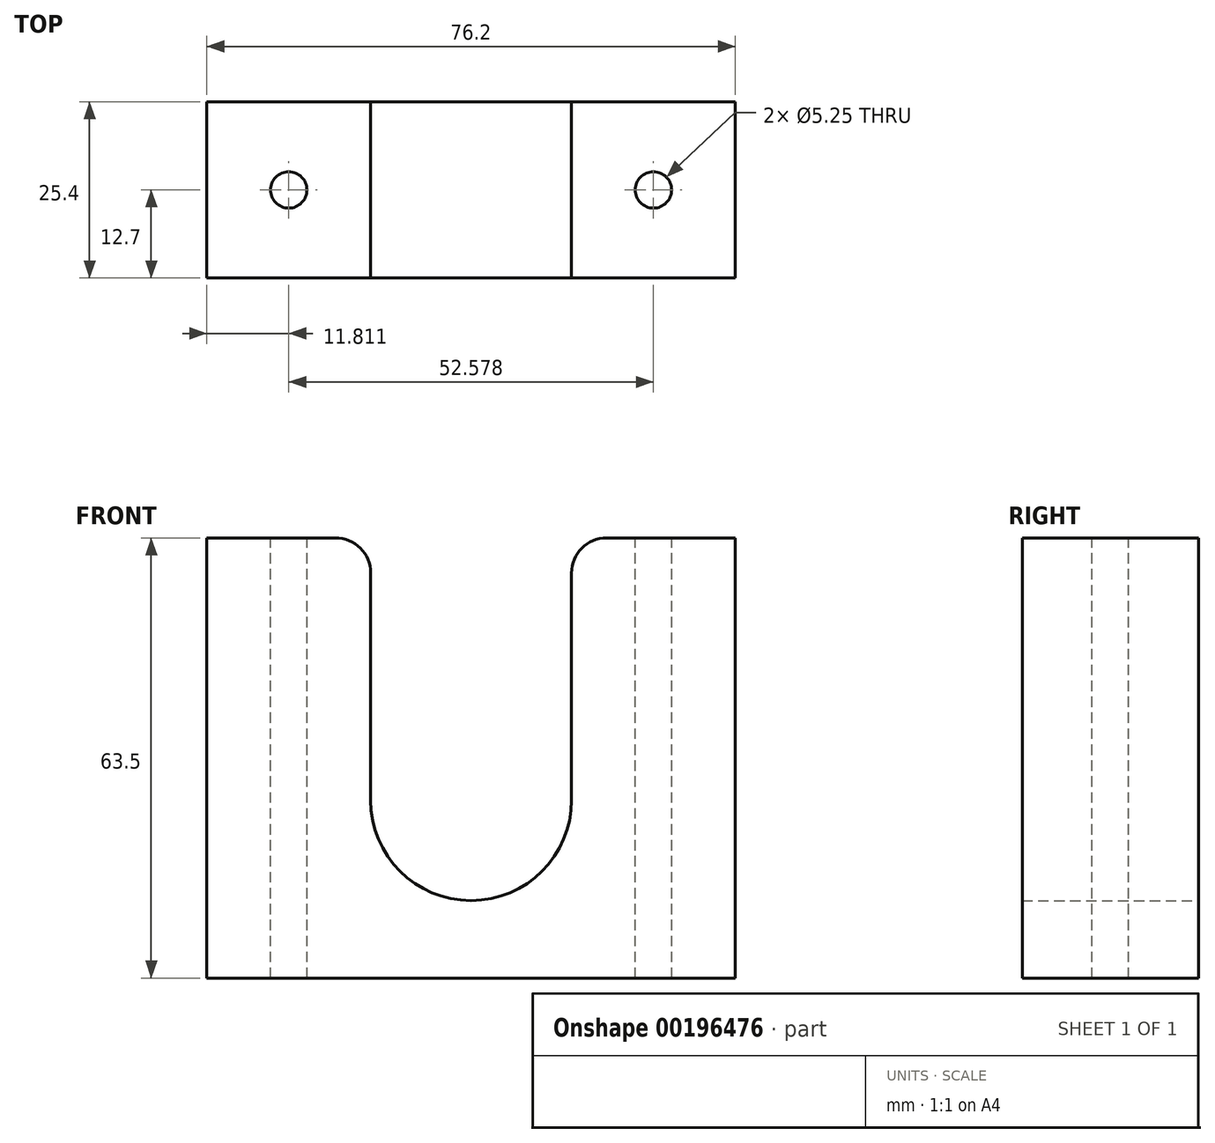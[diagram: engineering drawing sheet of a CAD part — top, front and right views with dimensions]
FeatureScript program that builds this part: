
annotation { "Feature Type Name" : "Feature", "Feature Type Description" : "" }
export const myFeature = defineFeature(function(context is Context, id is Id, definition is map)
    precondition{}
    {
        {
            var Q0;
            Q0=qCreatedBy(makeId("Front.planeOp"),FACE);
            var sketch = newSketch(context, id + "F0", { "sketchPlane" : qUnion([Q0])});
            skLineSegment(sketch, "E0.bottom", {"start": v(0, 0) * mm, "end": v(76.2, 0) * mm});
            skLineSegment(sketch, "E0.left", {"start": v(0, 0) * mm, "end": v(0, 63.5) * mm});
            skLineSegment(sketch, "E0.right", {"start": v(76.2, 0) * mm, "end": v(76.2, 63.5) * mm});
            skLineSegment(sketch, "E1", {"start": v(0, 63.5) * mm, "end": v(23.62, 63.5) * mm});
            skLineSegment(sketch, "E2", {"start": v(76.2, 63.5) * mm, "end": v(52.58, 63.5) * mm});
            skLineSegment(sketch, "E3", {"start": v(23.62, 63.5) * mm, "end": v(23.62, 25.65) * mm});
            skLineSegment(sketch, "E4", {"start": v(52.58, 63.5) * mm, "end": v(52.58, 25.65) * mm});
            skArc(sketch, "E5", {"start": v(23.62, 25.65) * mm, "mid": v(38.1, 11.18) * mm, "end": v(52.58, 25.65) * mm});
            skSolve(sketch);
        }
        {
            var Q0;
            Q0 = qSketchRegion(id + "F0", true);
            extrude(context, id + "F1", {"entities" : qUnion([Q0]), "depth" : 25.4 * mm});
        }
        {
            var Q0;
            Q0=makeQuery(id+"F1.opExtrude","SWEPT_FACE",FACE,{"disambiguationData":[OSD([sQuery(id+"F0.wireOp",EDGE,"E1")])]});
            var sketch = newSketch(context, id + "F2", { "sketchPlane" : qUnion([Q0])});
            skLineSegment(sketch, "E6", {"start": v(0, 0) * mm, "end": v(23.62, -25.4) * mm, "construction": true});
            skLineSegment(sketch, "E7", {"start": v(23.62, 0) * mm, "end": v(0, -25.4) * mm, "construction": true});
            skPoint(sketch, "E8", {"position": v(11.81, -12.7) * mm});
            skSolve(sketch);
        }
        {
            var Q0;
            Q0=makeQuery(id+"F1.opExtrude","SWEPT_FACE",FACE,{"disambiguationData":[OSD([sQuery(id+"F0.wireOp",EDGE,"E2")])]});
            var sketch = newSketch(context, id + "F3", { "sketchPlane" : qUnion([Q0])});
            skLineSegment(sketch, "E9", {"start": v(52.58, 0) * mm, "end": v(76.2, -25.4) * mm, "construction": true});
            skLineSegment(sketch, "E10", {"start": v(76.2, 0) * mm, "end": v(52.58, -25.4) * mm, "construction": true});
            skPoint(sketch, "E11", {"position": v(64.39, -12.7) * mm});
            skSolve(sketch);
        }
        {
            var Q0;
            Q0=sQuery(id+"F2.wireOp",VERTEX,"E8");
            var Q1;
            Q1=sQuery(id+"F3.wireOp",VERTEX,"E11");
            var Q2;
            Q2=makeQuery(id+"F1.opExtrude","SWEPT_BODY",BODY,{"disambiguationData":[OSD([sQuery(id+"F0.wireOp",EDGE,"E0.bottom"),sQuery(id+"F0.wireOp",EDGE,"E0.left"),sQuery(id+"F0.wireOp",EDGE,"E0.right"),sQuery(id+"F0.wireOp",EDGE,"E1"),sQuery(id+"F0.wireOp",EDGE,"E2"),sQuery(id+"F0.wireOp",EDGE,"E3"),sQuery(id+"F0.wireOp",EDGE,"E4"),sQuery(id+"F0.wireOp",EDGE,"E5")])]});
            hole(context, id + "F4", {"style" : HoleStyle.SIMPLE, "endStyle" : HoleEndStyle.THROUGH, "standardTappedOrClearance" : lookupTablePath({ "standard" : "ISO", "engagement" : "75%", "pitch" : "0.75 mm", "size" : "M6", "type" : "Tapped" }), "standardBlindInLast" : lookupTablePath({ "standard" : "ISO", "engagement" : "75%", "pitch" : "0.75 mm", "size" : "M6", "type" : "Tapped" }), "holeDiameter" : 5.25 * mm, "startFromSketch" : true, "locations" : qUnion([Q0, Q1]), "scope" : qUnion([Q2]), "isTappedThrough" : true, "majorDiameter" : 6 * mm, "showTappedDepth" : true});
        }
        {
            var Q0;
            Q0=makeQuery(id+"F1.opExtrude","SWEPT_EDGE",EDGE,{"disambiguationData":[OSD([sQuery(id+"F0.wireOp",EDGE,"E1"),sQuery(id+"F0.wireOp",EDGE,"E3")])]});
            var Q1;
            Q1=makeQuery(id+"F1.opExtrude","SWEPT_EDGE",EDGE,{"disambiguationData":[OSD([sQuery(id+"F0.wireOp",EDGE,"E2"),sQuery(id+"F0.wireOp",EDGE,"E4")])]});
            fillet(context, id + "F5", {"entities" : qUnion([Q0, Q1]), "radius" : 5.08 * mm, "tangentPropagation" : true, "allowEdgeOverflow" : false});
        }
    });
